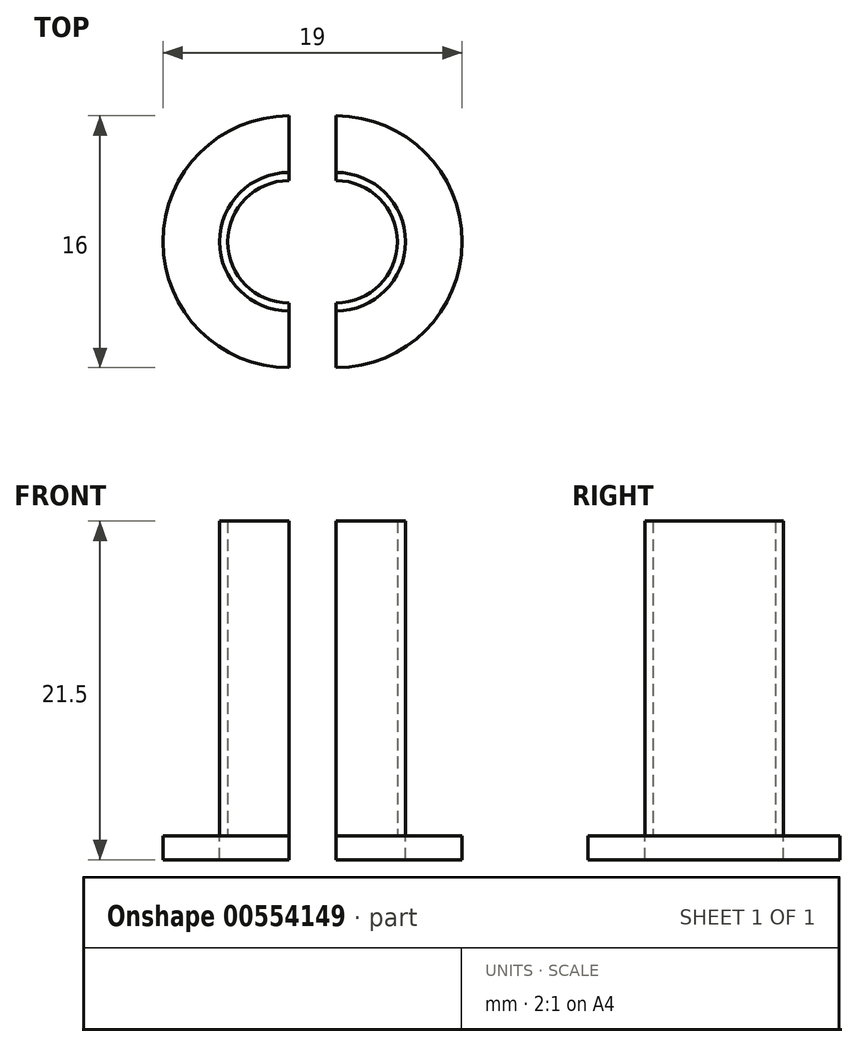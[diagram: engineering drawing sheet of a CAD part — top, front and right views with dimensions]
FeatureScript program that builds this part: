
annotation { "Feature Type Name" : "Feature", "Feature Type Description" : "" }
export const myFeature = defineFeature(function(context is Context, id is Id, definition is map)
    precondition{}
    {
        {
            var Q0;
            Q0=qCreatedBy(makeId("Top.planeOp"),FACE);
            var sketch = newSketch(context, id + "F0", { "sketchPlane" : qUnion([Q0])});
            skArc(sketch, "E0", {"start": v(0, 3.89) * mm, "mid": v(-3.89, 0) * mm, "end": v(0, -3.89) * mm});
            skArc(sketch, "E1", {"start": v(0, 4.4) * mm, "mid": v(-4.4, 0) * mm, "end": v(0, -4.4) * mm});
            skLineSegment(sketch, "E2", {"start": v(0, 8.54) * mm, "end": v(0, -6.78) * mm});
            skSolve(sketch);
        }
        {
            var Q0;
            Q0=makeQuery(id+"F0.imprint","IMPRINT",FACE,{"disambiguationData":[TD([[makeQuery(id+"F0.imprint","IMPRINT",EDGE,{"derivedFrom":sQuery(id+"F0.wireOp",EDGE,"E0")}),-1.0]])]});
            extrude(context, id + "F1", {"entities" : qUnion([Q0]), "depth" : 20 * mm, "offsetDistance" : 25 * mm});
        }
        {
            var Q0;
            Q0=makeQuery(id+"F1.opExtrude","CAP_FACE",FACE,{"disambiguationData":[OSD([sQuery(id+"F0.wireOp",EDGE,"E0"),sQuery(id+"F0.wireOp",EDGE,"E1"),sQuery(id+"F0.wireOp",EDGE,"E2")])],"isStart":true});
            var sketch = newSketch(context, id + "F2", { "sketchPlane" : qUnion([Q0])});
            skArc(sketch, "E3", {"start": v(0, 8) * mm, "mid": v(-8, 0) * mm, "end": v(0, -8) * mm});
            skLineSegment(sketch, "E4", {"start": v(0, 8.77) * mm, "end": v(0, -11.09) * mm});
            skSolve(sketch);
        }
        {
            var Q0;
            {var subQ0=sQuery(id+"F2.wireOp",EDGE,"E3");Q0=makeQuery(id+"F2.imprint","IMPRINT",FACE,{"disambiguationData":[TD([[makeQuery(id+"F2.imprint","IMPRINT",EDGE,{"derivedFrom":subQ0}),1.0]])]});}
            extrude(context, id + "F3", {"entities" : qUnion([Q0]), "depth" : 1.5 * mm, "offsetDistance" : 25 * mm});
        }
        {
            var Q0;
            Q0=makeQuery(id+"F3.opExtrude","SWEPT_BODY",BODY,{"disambiguationData":[OSD([sQuery(id+"F0.wireOp",EDGE,"E1"),sQuery(id+"F2.wireOp",EDGE,"E3"),sQuery(id+"F2.wireOp",EDGE,"E4")])]});
            var Q1;
            Q1=makeQuery(id+"F1.opExtrude","SWEPT_BODY",BODY,{"disambiguationData":[OSD([sQuery(id+"F0.wireOp",EDGE,"E0"),sQuery(id+"F0.wireOp",EDGE,"E1"),sQuery(id+"F0.wireOp",EDGE,"E2")])]});
            var Q2;
            Q2=qCreatedBy(makeId("Right.planeOp"),FACE);
            mirror(context, id + "F4", {"entities" : qUnion([Q0, Q1]), "mirrorPlane" : qUnion([Q2])});
        }
        {
            var Q0;
            Q0=makeQuery(id+"F4.opPattern","COPY",BODY,{"derivedFrom":makeQuery(id+"F3.opExtrude","SWEPT_BODY",BODY,{"disambiguationData":[OSD([sQuery(id+"F0.wireOp",EDGE,"E1"),sQuery(id+"F2.wireOp",EDGE,"E3"),sQuery(id+"F2.wireOp",EDGE,"E4")])]}),"instanceName":"1"});
            var Q1;
            Q1=makeQuery(id+"F4.opPattern","COPY",BODY,{"derivedFrom":makeQuery(id+"F1.opExtrude","SWEPT_BODY",BODY,{"disambiguationData":[OSD([sQuery(id+"F0.wireOp",EDGE,"E0"),sQuery(id+"F0.wireOp",EDGE,"E1"),sQuery(id+"F0.wireOp",EDGE,"E2")])]}),"instanceName":"1"});
            transform(context, id + "F5", {"entities" : qUnion([Q0, Q1]), "transformType" : TransformType.TRANSLATION_3D, "dx" : 3 * mm, "dy" : 0 * mm, "dz" : 0 * mm, "makeCopy" : false});
        }
    });
